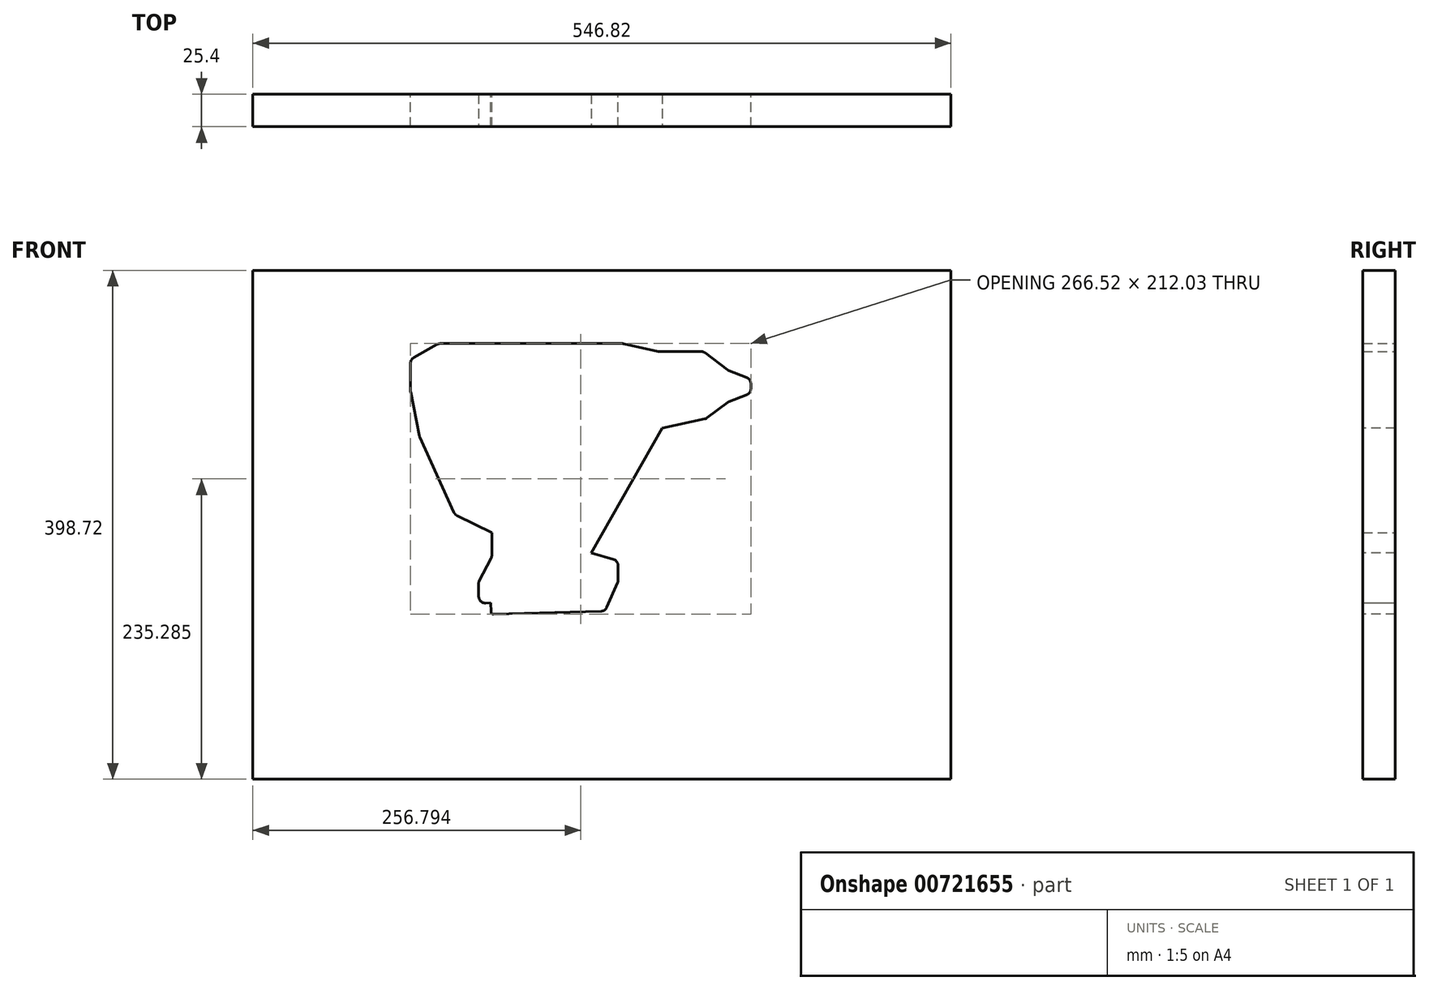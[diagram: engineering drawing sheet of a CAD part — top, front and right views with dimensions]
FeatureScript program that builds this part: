
annotation { "Feature Type Name" : "Feature", "Feature Type Description" : "" }
export const myFeature = defineFeature(function(context is Context, id is Id, definition is map)
    precondition{}
    {
        {
            var Q0;
            Q0=qCreatedBy(makeId("Front.planeOp"),FACE);
            var sketch = newSketch(context, id + "F0", { "sketchPlane" : qUnion([Q0])});
            skLineSegment(sketch, "E0", {"start": v(352.7, 58.78) * mm, "end": v(497.11, 58.78) * mm});
            skLineSegment(sketch, "E1", {"start": v(497.11, 58.78) * mm, "end": v(525.06, 52.57) * mm});
            skLineSegment(sketch, "E2", {"start": v(525.06, 52.57) * mm, "end": v(560, 52.57) * mm});
            skLineSegment(sketch, "E3", {"start": v(560, 52.57) * mm, "end": v(579.41, 37.82) * mm});
            skLineSegment(sketch, "E4", {"start": v(579.41, 37.82) * mm, "end": v(597.27, 30.83) * mm});
            skLineSegment(sketch, "E5", {"start": v(597.27, 30.83) * mm, "end": v(597.27, 19.96) * mm});
            skLineSegment(sketch, "E6", {"start": v(597.27, 19.96) * mm, "end": v(579.41, 12.97) * mm});
            skLineSegment(sketch, "E7", {"start": v(579.41, 12.97) * mm, "end": v(562.33, 0) * mm});
            skLineSegment(sketch, "E8", {"start": v(562.33, 0) * mm, "end": v(493.23, -14.98) * mm});
            skLineSegment(sketch, "E9", {"start": v(493.23, -14.98) * mm, "end": v(476.92, -48.37) * mm});
            skLineSegment(sketch, "E10", {"start": v(476.92, -48.37) * mm, "end": v(464.5, -54.58) * mm});
            skLineSegment(sketch, "E11", {"start": v(464.5, -54.58) * mm, "end": v(451.3, -98.84) * mm});
            skLineSegment(sketch, "E12", {"start": v(451.3, -98.84) * mm, "end": v(493.36, -111.38) * mm});
            skLineSegment(sketch, "E13", {"start": v(493.36, -111.38) * mm, "end": v(493.36, -127.57) * mm});
            skLineSegment(sketch, "E14", {"start": v(493.36, -127.57) * mm, "end": v(483.13, -150.86) * mm});
            skLineSegment(sketch, "E15", {"start": v(483.13, -150.86) * mm, "end": v(393.78, -153.3) * mm});
            skLineSegment(sketch, "E16", {"start": v(393.78, -153.3) * mm, "end": v(393.53, -144.37) * mm});
            skLineSegment(sketch, "E17", {"start": v(393.53, -144.37) * mm, "end": v(384.28, -144.63) * mm});
            skLineSegment(sketch, "E18", {"start": v(384.28, -144.63) * mm, "end": v(383.85, -128.77) * mm});
            skLineSegment(sketch, "E19", {"start": v(383.85, -128.77) * mm, "end": v(394.41, -108.22) * mm});
            skLineSegment(sketch, "E20", {"start": v(394.41, -108.22) * mm, "end": v(394.41, -64.46) * mm});
            skLineSegment(sketch, "E21", {"start": v(394.41, -64.46) * mm, "end": v(400.62, -38.84) * mm});
            skLineSegment(sketch, "E22", {"start": v(400.62, -38.84) * mm, "end": v(368.01, -22.53) * mm});
            skLineSegment(sketch, "E23", {"start": v(368.01, -22.53) * mm, "end": v(337.8, -13.97) * mm});
            skLineSegment(sketch, "E24", {"start": v(337.8, -13.97) * mm, "end": v(330.76, 21.27) * mm});
            skLineSegment(sketch, "E25", {"start": v(330.76, 21.27) * mm, "end": v(330.76, 46.42) * mm});
            skLineSegment(sketch, "E26", {"start": v(330.76, 46.42) * mm, "end": v(352.7, 58.78) * mm});
            skLineSegment(sketch, "E27.bottom", {"start": v(207.22, 116.2) * mm, "end": v(754.04, 116.2) * mm});
            skLineSegment(sketch, "E27.top", {"start": v(207.22, -282.52) * mm, "end": v(754.04, -282.52) * mm});
            skLineSegment(sketch, "E27.left", {"start": v(207.22, 116.2) * mm, "end": v(207.22, -282.52) * mm});
            skLineSegment(sketch, "E27.right", {"start": v(754.04, 116.2) * mm, "end": v(754.04, -282.52) * mm});
            skSolve(sketch);
        }
        {
            var Q0;
            Q0 = qSketchRegion(id + "F0", true);
            extrude(context, id + "F1", {"entities" : qUnion([Q0]), "depth" : 25.4 * mm, "offsetDistance" : 25.4 * mm});
        }
        {
            var Q0;
            Q0=makeQuery(id+"F1.opExtrude","CAP_FACE",FACE,{"disambiguationData":[OSD([sQuery(id+"F0.wireOp",EDGE,"E0"),sQuery(id+"F0.wireOp",EDGE,"E1"),sQuery(id+"F0.wireOp",EDGE,"E2"),sQuery(id+"F0.wireOp",EDGE,"E3"),sQuery(id+"F0.wireOp",EDGE,"E4"),sQuery(id+"F0.wireOp",EDGE,"E5"),sQuery(id+"F0.wireOp",EDGE,"E6"),sQuery(id+"F0.wireOp",EDGE,"E7"),sQuery(id+"F0.wireOp",EDGE,"E8"),sQuery(id+"F0.wireOp",EDGE,"E9"),sQuery(id+"F0.wireOp",EDGE,"E10"),sQuery(id+"F0.wireOp",EDGE,"E11"),sQuery(id+"F0.wireOp",EDGE,"E12"),sQuery(id+"F0.wireOp",EDGE,"E13"),sQuery(id+"F0.wireOp",EDGE,"E14"),sQuery(id+"F0.wireOp",EDGE,"E15"),sQuery(id+"F0.wireOp",EDGE,"E16"),sQuery(id+"F0.wireOp",EDGE,"E17"),sQuery(id+"F0.wireOp",EDGE,"E18"),sQuery(id+"F0.wireOp",EDGE,"E19"),sQuery(id+"F0.wireOp",EDGE,"E20"),sQuery(id+"F0.wireOp",EDGE,"E21"),sQuery(id+"F0.wireOp",EDGE,"E22"),sQuery(id+"F0.wireOp",EDGE,"E23"),sQuery(id+"F0.wireOp",EDGE,"E24"),sQuery(id+"F0.wireOp",EDGE,"E25"),sQuery(id+"F0.wireOp",EDGE,"E26"),sQuery(id+"F0.wireOp",EDGE,"E27.bottom"),sQuery(id+"F0.wireOp",EDGE,"E27.top"),sQuery(id+"F0.wireOp",EDGE,"E27.left"),sQuery(id+"F0.wireOp",EDGE,"E27.right")])],"isStart":false});
            var sketch = newSketch(context, id + "F2", { "sketchPlane" : qUnion([Q0])});
            skLineSegment(sketch, "E28", {"start": v(337.8, -13.97) * mm, "end": v(527.78, -7.5) * mm});
            skLineSegment(sketch, "E29", {"start": v(472.33, -105.1) * mm, "end": v(527.78, -7.5) * mm});
            skLineSegment(sketch, "E30", {"start": v(472.33, -105.1) * mm, "end": v(401.74, -93.16) * mm});
            skLineSegment(sketch, "E31", {"start": v(401.74, -93.16) * mm, "end": v(365.54, -75.13) * mm});
            skLineSegment(sketch, "E32", {"start": v(365.54, -75.13) * mm, "end": v(337.8, -13.97) * mm});
            skSolve(sketch);
        }
        {
            var Q0;
            Q0 = qSketchRegion(id + "F2", true);
            extrude(context, id + "F3", {"entities" : qUnion([Q0]), "operationType" : NewBodyOperationType.REMOVE, "endBound" : BoundingType.THROUGH_ALL, "oppositeDirection" : true, "depth" : 25.4 * mm, "offsetDistance" : 25.4 * mm});
        }
        {
            var Q0;
            Q0=makeQuery(id+"F1.opExtrude","SWEPT_EDGE",EDGE,{"disambiguationData":[OSD([sQuery(id+"F0.wireOp",EDGE,"E24"),sQuery(id+"F0.wireOp",EDGE,"E25")])]});
            var Q1;
            Q1=makeQuery(id+"F1.opExtrude","SWEPT_EDGE",EDGE,{"disambiguationData":[OSD([sQuery(id+"F0.wireOp",EDGE,"E25"),sQuery(id+"F0.wireOp",EDGE,"E26")])]});
            var Q2;
            Q2=makeQuery(id+"F1.opExtrude","SWEPT_EDGE",EDGE,{"disambiguationData":[OSD([sQuery(id+"F0.wireOp",EDGE,"E0"),sQuery(id+"F0.wireOp",EDGE,"E26")])]});
            var Q3;
            {var subQ0=sQuery(id+"F0.wireOp",EDGE,"E24");var subQ1=sQuery(id+"F0.wireOp",EDGE,"E23");Q3=makeQuery(id+"F3.boolean.opBoolean","MERGE",EDGE,{"derivedFrom":[makeQuery(id+"F1.opExtrude","SWEPT_EDGE",EDGE,{"disambiguationData":[OSD([subQ1,subQ0])]}),makeQuery(id+"F3.opExtrude","SWEPT_EDGE",EDGE,{"disambiguationData":[OSD([subQ1,subQ0,sQuery(id+"F2.wireOp",EDGE,"E28"),sQuery(id+"F2.wireOp",EDGE,"5ajZNRRd-wZbH-desb-TgtO-Uh6JfcWsMo07")])]})]});}
            var Q4;
            Q4=makeQuery(id+"F3.boolean.opBoolean","COPY",EDGE,{"derivedFrom":makeQuery(id+"F3.opExtrude","SWEPT_EDGE",EDGE,{"disambiguationData":[OSD([sQuery(id+"F2.wireOp",EDGE,"E28"),sQuery(id+"F2.wireOp",EDGE,"8tqHyfO4-ZUus-Q0xi-IMOL-LWRtgQ276f3c")])]})});
            var Q5;
            Q5=makeQuery(id+"F3.boolean.opBoolean","INTERSECT",EDGE,{"derivedFrom":[makeQuery(id+"F1.opExtrude","SWEPT_FACE",FACE,{"disambiguationData":[OSD([sQuery(id+"F0.wireOp",EDGE,"E20")])]}),makeQuery(id+"F3.opExtrude","SWEPT_FACE",FACE,{"disambiguationData":[OSD([sQuery(id+"F2.wireOp",EDGE,"8tqHyfO4-ZUus-Q0xi-IMOL-LWRtgQ276f3c")])]})]});
            var Q6;
            Q6=makeQuery(id+"F1.opExtrude","SWEPT_EDGE",EDGE,{"disambiguationData":[OSD([sQuery(id+"F0.wireOp",EDGE,"E19"),sQuery(id+"F0.wireOp",EDGE,"E20")])]});
            var Q7;
            Q7=makeQuery(id+"F1.opExtrude","SWEPT_EDGE",EDGE,{"disambiguationData":[OSD([sQuery(id+"F0.wireOp",EDGE,"E18"),sQuery(id+"F0.wireOp",EDGE,"E19")])]});
            var Q8;
            Q8=makeQuery(id+"F1.opExtrude","SWEPT_EDGE",EDGE,{"disambiguationData":[OSD([sQuery(id+"F0.wireOp",EDGE,"E17"),sQuery(id+"F0.wireOp",EDGE,"E18")])]});
            var Q9;
            Q9=makeQuery(id+"F1.opExtrude","SWEPT_EDGE",EDGE,{"disambiguationData":[OSD([sQuery(id+"F0.wireOp",EDGE,"E14"),sQuery(id+"F0.wireOp",EDGE,"E15")])]});
            var Q10;
            Q10=makeQuery(id+"F1.opExtrude","SWEPT_EDGE",EDGE,{"disambiguationData":[OSD([sQuery(id+"F0.wireOp",EDGE,"E13"),sQuery(id+"F0.wireOp",EDGE,"E14")])]});
            var Q11;
            Q11=makeQuery(id+"F3.boolean.opBoolean","COPY",EDGE,{"derivedFrom":makeQuery(id+"F3.opExtrude","SWEPT_EDGE",EDGE,{"disambiguationData":[OSD([sQuery(id+"F0.wireOp",EDGE,"E8"),sQuery(id+"F2.wireOp",EDGE,"f09YN0uh-BKY4-7GqD-z0pc-ekR8PJXDGYGa"),sQuery(id+"F2.wireOp",EDGE,"5ajZNRRd-wZbH-desb-TgtO-Uh6JfcWsMo07")])]})});
            var Q12;
            Q12=makeQuery(id+"F1.opExtrude","SWEPT_EDGE",EDGE,{"disambiguationData":[OSD([sQuery(id+"F0.wireOp",EDGE,"E7"),sQuery(id+"F0.wireOp",EDGE,"E8")])]});
            var Q13;
            Q13=makeQuery(id+"F1.opExtrude","SWEPT_EDGE",EDGE,{"disambiguationData":[OSD([sQuery(id+"F0.wireOp",EDGE,"E6"),sQuery(id+"F0.wireOp",EDGE,"E7")])]});
            var Q14;
            Q14=makeQuery(id+"F1.opExtrude","SWEPT_EDGE",EDGE,{"disambiguationData":[OSD([sQuery(id+"F0.wireOp",EDGE,"E5"),sQuery(id+"F0.wireOp",EDGE,"E6")])]});
            var Q15;
            Q15=makeQuery(id+"F1.opExtrude","SWEPT_EDGE",EDGE,{"disambiguationData":[OSD([sQuery(id+"F0.wireOp",EDGE,"E12"),sQuery(id+"F0.wireOp",EDGE,"E13")])]});
            var Q16;
            Q16=makeQuery(id+"F1.opExtrude","SWEPT_EDGE",EDGE,{"disambiguationData":[OSD([sQuery(id+"F0.wireOp",EDGE,"E1"),sQuery(id+"F0.wireOp",EDGE,"E2")])]});
            var Q17;
            Q17=makeQuery(id+"F1.opExtrude","SWEPT_EDGE",EDGE,{"disambiguationData":[OSD([sQuery(id+"F0.wireOp",EDGE,"E2"),sQuery(id+"F0.wireOp",EDGE,"E3")])]});
            var Q18;
            Q18=makeQuery(id+"F1.opExtrude","SWEPT_EDGE",EDGE,{"disambiguationData":[OSD([sQuery(id+"F0.wireOp",EDGE,"E3"),sQuery(id+"F0.wireOp",EDGE,"E4")])]});
            var Q19;
            Q19=makeQuery(id+"F1.opExtrude","SWEPT_EDGE",EDGE,{"disambiguationData":[OSD([sQuery(id+"F0.wireOp",EDGE,"E4"),sQuery(id+"F0.wireOp",EDGE,"E5")])]});
            var Q20;
            Q20=makeQuery(id+"F1.opExtrude","SWEPT_EDGE",EDGE,{"disambiguationData":[OSD([sQuery(id+"F0.wireOp",EDGE,"E0"),sQuery(id+"F0.wireOp",EDGE,"E1")])]});
            var Q21;
            Q21=makeQuery(id+"F3.boolean.opBoolean","COPY",EDGE,{"derivedFrom":makeQuery(id+"F3.opExtrude","SWEPT_EDGE",EDGE,{"disambiguationData":[OSD([sQuery(id+"F2.wireOp",EDGE,"E31"),sQuery(id+"F2.wireOp",EDGE,"E32")])]})});
            var Q22;
            Q22=makeQuery(id+"F3.boolean.opBoolean","COPY",EDGE,{"derivedFrom":makeQuery(id+"F3.opExtrude","SWEPT_EDGE",EDGE,{"disambiguationData":[OSD([sQuery(id+"F0.wireOp",EDGE,"E12"),sQuery(id+"F2.wireOp",EDGE,"E29"),sQuery(id+"F2.wireOp",EDGE,"E30")])]})});
            fillet(context, id + "F4", {"entities" : qUnion([Q0, Q1, Q2, Q3, Q4, Q5, Q6, Q7, Q8, Q9, Q10, Q11, Q12, Q13, Q14, Q15, Q16, Q17, Q18, Q19, Q20, Q21, Q22]), "radius" : 5.08 * mm, "tangentPropagation" : true, "allowEdgeOverflow" : false});
        }
        {
            var Q0;
            Q0=makeQuery(id+"F4.opFillet","BLEND_EDGE",EDGE,{"blendedFrom":[makeQuery(id+"F1.opExtrude","SWEPT_EDGE",EDGE,{"disambiguationData":[OSD([sQuery(id+"F0.wireOp",EDGE,"E17"),sQuery(id+"F0.wireOp",EDGE,"E18")])]}),makeQuery(id+"F1.opExtrude","SWEPT_FACE",FACE,{"disambiguationData":[OSD([sQuery(id+"F0.wireOp",EDGE,"E16")])]})],"blendedInto":[makeQuery(id+"F1.opExtrude","SWEPT_FACE",FACE,{"disambiguationData":[OSD([sQuery(id+"F0.wireOp",EDGE,"E16")])]})]});
            var Q1;
            Q1=makeQuery(id+"F3.boolean.opBoolean","INTERSECT",EDGE,{"derivedFrom":[makeQuery(id+"F1.opExtrude","SWEPT_FACE",FACE,{"disambiguationData":[OSD([sQuery(id+"F0.wireOp",EDGE,"E12")])]}),makeQuery(id+"F3.opExtrude","SWEPT_FACE",FACE,{"disambiguationData":[OSD([sQuery(id+"F2.wireOp",EDGE,"f09YN0uh-BKY4-7GqD-z0pc-ekR8PJXDGYGa")])]})]});
            var Q2;
            Q2=makeQuery(id+"F1.opExtrude","SWEPT_EDGE",EDGE,{"disambiguationData":[OSD([sQuery(id+"F0.wireOp",EDGE,"E15"),sQuery(id+"F0.wireOp",EDGE,"E16")])]});
            fillet(context, id + "F5", {"entities" : qUnion([Q0, Q1, Q2]), "radius" : 2.16 * mm, "tangentPropagation" : true, "allowEdgeOverflow" : false});
        }
    });
